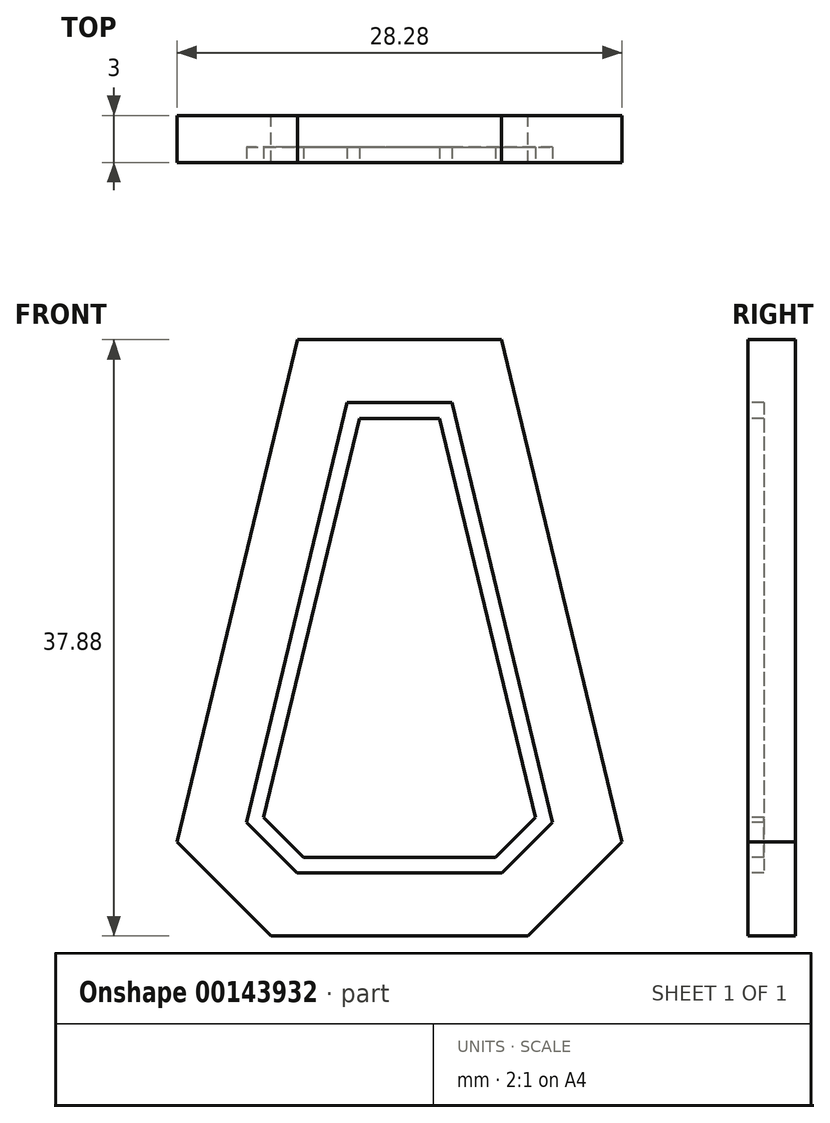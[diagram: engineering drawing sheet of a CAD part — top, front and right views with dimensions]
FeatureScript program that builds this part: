
annotation { "Feature Type Name" : "Feature", "Feature Type Description" : "" }
export const myFeature = defineFeature(function(context is Context, id is Id, definition is map)
    precondition{}
    {
        {
            var Q0;
            Q0=qCreatedBy(makeId("Front.planeOp"),FACE);
            cPlane(context, id + "F0", {"entities" : qUnion([Q0]), "cplaneType" : CPlaneType.OFFSET, "offset" : 23 * mm, "width" : 150 * mm, "height" : 150 * mm});
        }
        {
            var Q0;
            Q0=qCreatedBy(id+"F0.planeOp",FACE);
            var sketch = newSketch(context, id + "F1", { "sketchPlane" : qUnion([Q0])});
            skLineSegment(sketch, "E0.0", {"start": v(-14.14, -44.91) * mm, "end": v(-6.48, -13) * mm});
            skLineSegment(sketch, "E1.0", {"start": v(6.48, -13) * mm, "end": v(-6.48, -13) * mm});
            skLineSegment(sketch, "E2.0", {"start": v(14.14, -44.91) * mm, "end": v(6.48, -13) * mm});
            skLineSegment(sketch, "E3.0", {"start": v(8.17, -50.88) * mm, "end": v(14.14, -44.91) * mm});
            skLineSegment(sketch, "E4.0", {"start": v(-8.17, -50.88) * mm, "end": v(-14.14, -44.91) * mm});
            skLineSegment(sketch, "E5.0", {"start": v(-8.17, -50.88) * mm, "end": v(8.17, -50.88) * mm});
            skSolve(sketch);
        }
        {
            var Q0;
            Q0 = qSketchRegion(id + "F1", true);
            extrude(context, id + "F2", {"entities" : qUnion([Q0]), "depth" : 3 * mm});
        }
        {
            var Q0;
            Q0=makeQuery(id+"F2.opExtrude","CAP_FACE",FACE,{"disambiguationData":[OSD([sQuery(id+"F1.wireOp",EDGE,"E0.0"),sQuery(id+"F1.wireOp",EDGE,"E1.0"),sQuery(id+"F1.wireOp",EDGE,"E2.0"),sQuery(id+"F1.wireOp",EDGE,"E3.0"),sQuery(id+"F1.wireOp",EDGE,"E4.0"),sQuery(id+"F1.wireOp",EDGE,"E5.0")])],"isStart":false});
            var sketch = newSketch(context, id + "F3", { "sketchPlane" : qUnion([Q0])});
            skLineSegment(sketch, "E6.0", {"start": v(2.54, -18) * mm, "end": v(-2.54, -18) * mm});
            skLineSegment(sketch, "E6.1", {"start": v(-8.62, -43.36) * mm, "end": v(-6.1, -45.88) * mm});
            skLineSegment(sketch, "E6.2", {"start": v(-6.1, -45.88) * mm, "end": v(6.1, -45.88) * mm});
            skLineSegment(sketch, "E6.3", {"start": v(-2.54, -18) * mm, "end": v(-8.62, -43.36) * mm});
            skLineSegment(sketch, "E6.4", {"start": v(6.1, -45.88) * mm, "end": v(8.62, -43.36) * mm});
            skLineSegment(sketch, "E6.5", {"start": v(8.62, -43.36) * mm, "end": v(2.54, -18) * mm});
            skLineSegment(sketch, "E7.0", {"start": v(3.33, -17) * mm, "end": v(-3.33, -17) * mm});
            skLineSegment(sketch, "E7.1", {"start": v(-9.73, -43.67) * mm, "end": v(-6.51, -46.88) * mm});
            skLineSegment(sketch, "E7.2", {"start": v(-6.51, -46.88) * mm, "end": v(6.51, -46.88) * mm});
            skLineSegment(sketch, "E7.3", {"start": v(-3.33, -17) * mm, "end": v(-9.73, -43.67) * mm});
            skLineSegment(sketch, "E7.4", {"start": v(6.51, -46.88) * mm, "end": v(9.73, -43.67) * mm});
            skLineSegment(sketch, "E7.5", {"start": v(9.73, -43.67) * mm, "end": v(3.33, -17) * mm});
            skSolve(sketch);
        }
        {
            var Q0;
            Q0 = qSketchRegion(id + "F3", true);
            extrude(context, id + "F4", {"entities" : qUnion([Q0]), "operationType" : NewBodyOperationType.REMOVE, "oppositeDirection" : true, "depth" : 1 * mm});
        }
    });
